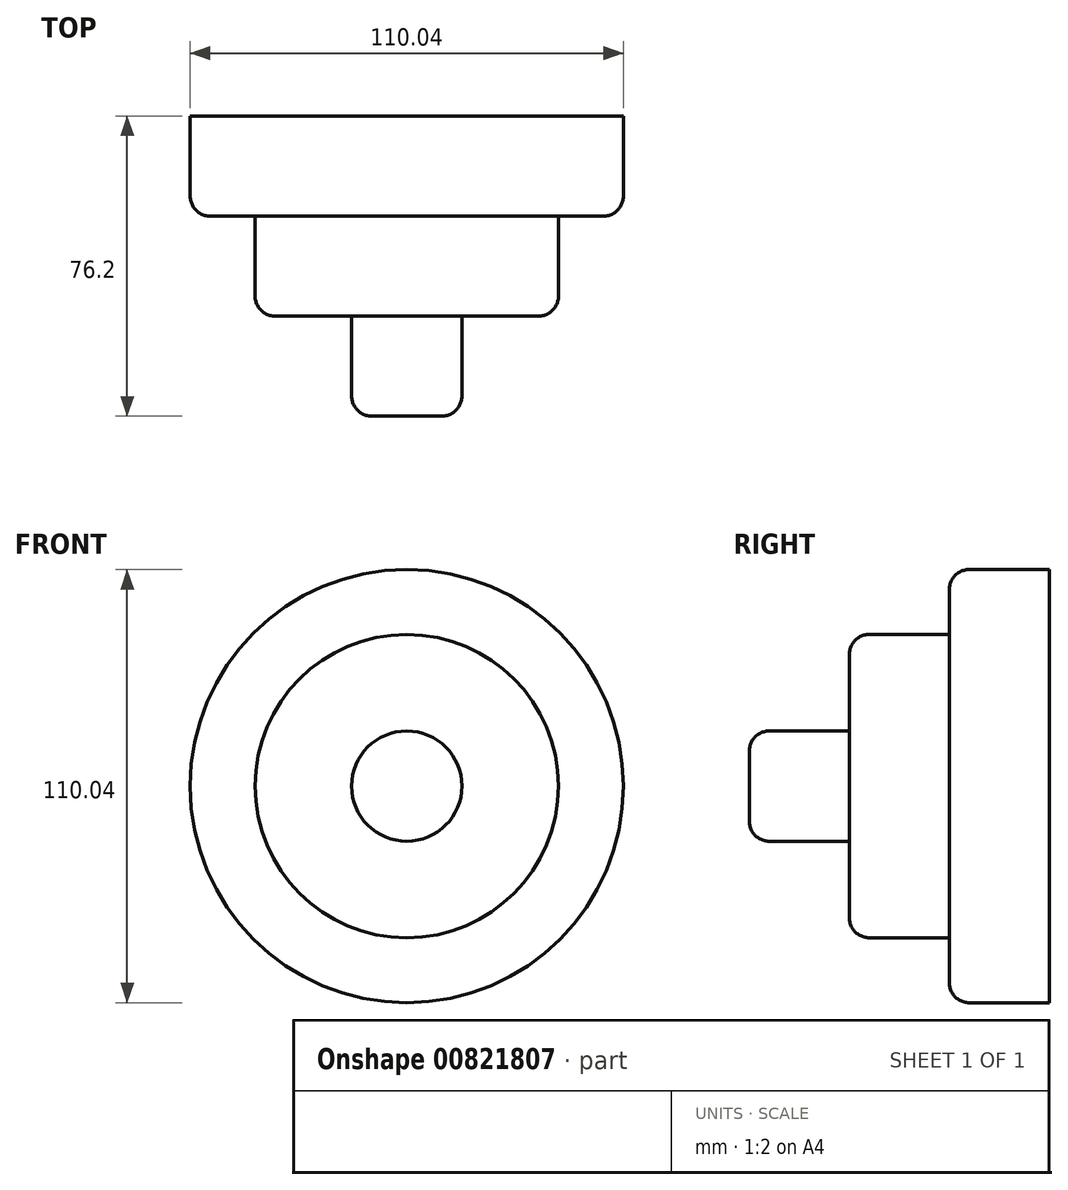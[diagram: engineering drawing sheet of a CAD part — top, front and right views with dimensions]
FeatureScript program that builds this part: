
annotation { "Feature Type Name" : "Feature", "Feature Type Description" : "" }
export const myFeature = defineFeature(function(context is Context, id is Id, definition is map)
    precondition{}
    {
        {
            var Q0;
            Q0=qCreatedBy(makeId("Front.planeOp"),FACE);
            var sketch = newSketch(context, id + "F0", { "sketchPlane" : qUnion([Q0])});
            skCircle(sketch, "E0", {"center": v(0, 0) * mm, "radius": 55.02 * mm});
            skSolve(sketch);
        }
        {
            var Q0;
            Q0 = qSketchRegion(id + "F0", true);
            extrude(context, id + "F1", {"entities" : qUnion([Q0]), "depth" : 25.4 * mm, "offsetDistance" : 25.4 * mm});
        }
        {
            var Q0;
            Q0=makeQuery(id+"F1.opExtrude","CAP_FACE",FACE,{"disambiguationData":[OSD([sQuery(id+"F0.wireOp",EDGE,"E0")])],"isStart":false});
            var sketch = newSketch(context, id + "F2", { "sketchPlane" : qUnion([Q0])});
            skCircle(sketch, "E1", {"center": v(0, 0) * mm, "radius": 38.53 * mm});
            skCircle(sketch, "E2", {"center": v(0, 0) * mm, "radius": 14 * mm});
            skSolve(sketch);
        }
        {
            var Q0;
            Q0=makeQuery(id+"F2.imprint","IMPRINT",FACE,{"disambiguationData":[TD([[makeQuery(id+"F2.imprint","IMPRINT",EDGE,{"derivedFrom":sQuery(id+"F2.wireOp",EDGE,"E1")}),1.0]])]});
            extrude(context, id + "F3", {"entities" : qUnion([Q0]), "operationType" : NewBodyOperationType.ADD, "depth" : 25.4 * mm, "offsetDistance" : 25.4 * mm});
        }
        {
            var Q0;
            Q0=makeQuery(id+"F1.opExtrude","CAP_EDGE",EDGE,{"disambiguationData":[OSD([sQuery(id+"F0.wireOp",EDGE,"E0")])],"isStart":false});
            var Q1;
            Q1=makeQuery(id+"F3.opExtrude","CAP_EDGE",EDGE,{"disambiguationData":[OSD([sQuery(id+"F2.wireOp",EDGE,"E1")])],"isStart":false});
            fillet(context, id + "F4", {"entities" : qUnion([Q0, Q1]), "radius" : 5.08 * mm, "tangentPropagation" : true, "allowEdgeOverflow" : false});
        }
        {
            var Q0;
            Q0=makeQuery(id+"F3.boolean.opBoolean","SPLIT",FACE,{"disambiguationData":[TD([makeQuery(id+"F3.opExtrude","SWEPT_FACE",FACE,{"disambiguationData":[OSD([sQuery(id+"F2.wireOp",EDGE,"E2")])]})])],"derivedFrom":makeQuery(id+"F1.opExtrude","CAP_FACE",FACE,{"disambiguationData":[OSD([sQuery(id+"F0.wireOp",EDGE,"E0")])],"isStart":false})});
            extrude(context, id + "F5", {"entities" : qUnion([Q0]), "operationType" : NewBodyOperationType.ADD, "depth" : 50.8 * mm, "offsetDistance" : 25.4 * mm});
        }
        {
            var Q0;
            Q0=makeQuery(id+"F5.opExtrude","CAP_EDGE",EDGE,{"disambiguationData":[OSD([sQuery(id+"F2.wireOp",EDGE,"E2")])],"isStart":false});
            fillet(context, id + "F6", {"entities" : qUnion([Q0]), "radius" : 5.08 * mm, "tangentPropagation" : true, "allowEdgeOverflow" : false});
        }
    });
